# Revit family: PLATI 216-SBC-216
name_source: partatom
category: Plumbing Fixtures
revit_build: Autodesk Revit 2017 (Build: 20171027_0315(x64)
units: mm (PartAtom-declared; Revit-internal decimal feet)

## family parameters
Always vertical = Yes
Cut with Voids When Loaded = No
OmniClass Number = 23.45.00.00
OmniClass Title = Sanitary, Laundry, and Cleaning Equipment
Part Type = Normal
Room Calculation Point = No
Round Connector Dimension = Use Diameter
Shared = No
Work Plane-Based = No

## types (1)
- PLATI 216-SBC-216
    Basin Material = white vitreous china, gloss finish.
    Description = The simple lines of this rectangular undermount basin will complement 
any bathroom design.  Suits solid surface benchtops.
    Manufacturer = SEIMA
    Model = PLATI SBC-216
    Steel = Steel
    Type Comments = The simple lines of this rectangular undermount basin will complement 
any bathroom design.  Suits solid surface benchtops.
    URL = www.seima.com.au
    Waste Connection = Yes
    Waste Size = 32 mm

## geometry (parser evidence)
native form markers: Sweep x2
no freeform markers — native parametric forms only
